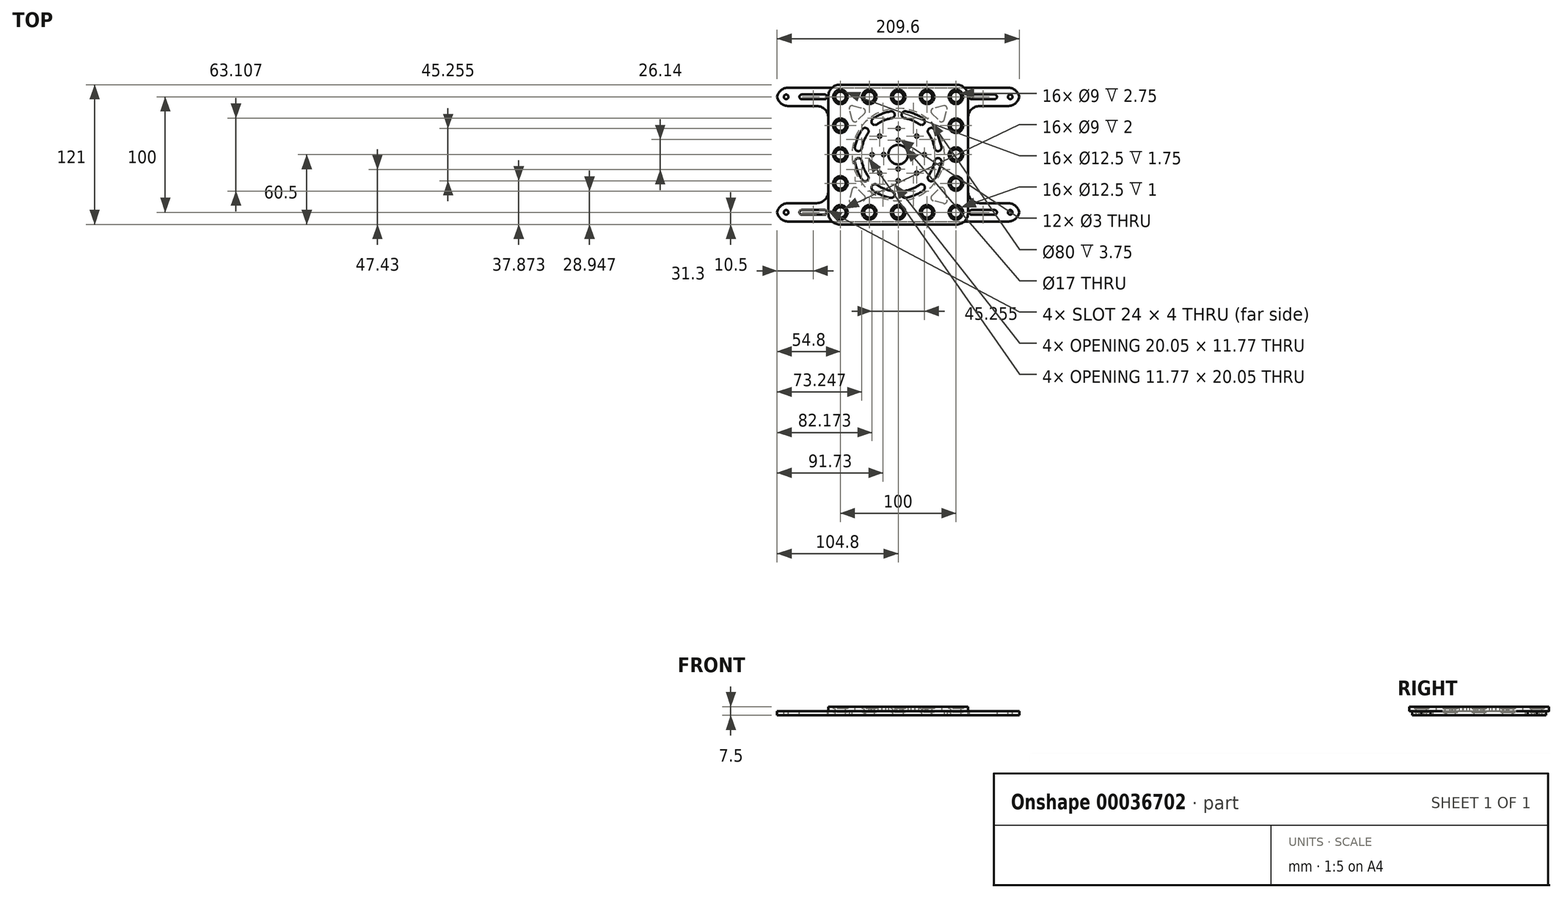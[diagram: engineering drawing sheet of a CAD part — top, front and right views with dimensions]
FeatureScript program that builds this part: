
annotation { "Feature Type Name" : "Feature", "Feature Type Description" : "" }
export const myFeature = defineFeature(function(context is Context, id is Id, definition is map)
    precondition{}
    {
        {
            var Q0;
            Q0=qCreatedBy(makeId("Top.planeOp"),FACE);
            var sketch = newSketch(context, id + "F0", { "sketchPlane" : qUnion([Q0])});
            skPoint(sketch, "E0.rect.middle", {"position": v(0, 0) * mm});
            skCircle(sketch, "E1", {"center": v(0, 0) * mm, "radius": 40 * mm});
            skLineSegment(sketch, "E2.rect.bottom", {"start": v(-50, 50) * mm, "end": v(50, 50) * mm, "construction": true});
            skLineSegment(sketch, "E2.rect.top", {"start": v(-50, -50) * mm, "end": v(50, -50) * mm, "construction": true});
            skLineSegment(sketch, "E2.rect.left", {"start": v(-50, 50) * mm, "end": v(-50, -50) * mm, "construction": true});
            skLineSegment(sketch, "E2.rect.right", {"start": v(50, 50) * mm, "end": v(50, -50) * mm, "construction": true});
            skCircle(sketch, "E3", {"center": v(-50, 50) * mm, "radius": 4.5 * mm});
            skCircle(sketch, "E4", {"center": v(50, 50) * mm, "radius": 4.5 * mm});
            skCircle(sketch, "E5", {"center": v(50, -50) * mm, "radius": 4.5 * mm});
            skCircle(sketch, "E6", {"center": v(-50, -50) * mm, "radius": 4.5 * mm});
            skCircle(sketch, "E7", {"center": v(0, -50) * mm, "radius": 4.5 * mm});
            skCircle(sketch, "E8", {"center": v(0, 50) * mm, "radius": 4.5 * mm});
            skCircle(sketch, "E9", {"center": v(50, 0) * mm, "radius": 4.5 * mm});
            skCircle(sketch, "E10", {"center": v(-50, 0) * mm, "radius": 4.5 * mm});
            skLineSegment(sketch, "E11.rect.bottom", {"start": v(-50, 25) * mm, "end": v(50, 25) * mm, "construction": true});
            skLineSegment(sketch, "E11.rect.top", {"start": v(-50, -25) * mm, "end": v(50, -25) * mm, "construction": true});
            skLineSegment(sketch, "E11.rect.left", {"start": v(-50, 25) * mm, "end": v(-50, -25) * mm, "construction": true});
            skLineSegment(sketch, "E11.rect.right", {"start": v(50, 25) * mm, "end": v(50, -25) * mm, "construction": true});
            skCircle(sketch, "E12", {"center": v(-50, 25) * mm, "radius": 4.5 * mm});
            skCircle(sketch, "E13", {"center": v(50, 25) * mm, "radius": 4.5 * mm});
            skCircle(sketch, "E14", {"center": v(50, -25) * mm, "radius": 4.5 * mm});
            skCircle(sketch, "E15", {"center": v(-50, -25) * mm, "radius": 4.5 * mm});
            skLineSegment(sketch, "E16.rect.bottom", {"start": v(-25, 50) * mm, "end": v(25, 50) * mm, "construction": true});
            skLineSegment(sketch, "E16.rect.top", {"start": v(-25, -50) * mm, "end": v(25, -50) * mm, "construction": true});
            skLineSegment(sketch, "E16.rect.left", {"start": v(-25, 50) * mm, "end": v(-25, -50) * mm, "construction": true});
            skLineSegment(sketch, "E16.rect.right", {"start": v(25, 50) * mm, "end": v(25, -50) * mm, "construction": true});
            skCircle(sketch, "E17", {"center": v(-25, 50) * mm, "radius": 4.5 * mm});
            skCircle(sketch, "E18", {"center": v(25, 50) * mm, "radius": 4.5 * mm});
            skCircle(sketch, "E19", {"center": v(25, -50) * mm, "radius": 4.5 * mm});
            skCircle(sketch, "E20", {"center": v(-25, -50) * mm, "radius": 4.5 * mm});
            skLineSegment(sketch, "E21.rect.bottom", {"start": v(-105, 58) * mm, "end": v(105, 58) * mm});
            skLineSegment(sketch, "E21.rect.top", {"start": v(-105, -58) * mm, "end": v(105, -58) * mm});
            skLineSegment(sketch, "E21.rect.left", {"start": v(-105, 58) * mm, "end": v(-105, 42) * mm});
            skLineSegment(sketch, "E21.rect.right", {"start": v(105, 58) * mm, "end": v(105, 42) * mm});
            skLineSegment(sketch, "E22.rect.bottom", {"start": v(-97, 50) * mm, "end": v(97, 50) * mm, "construction": true});
            skLineSegment(sketch, "E22.rect.top", {"start": v(-97, -50) * mm, "end": v(97, -50) * mm, "construction": true});
            skLineSegment(sketch, "E22.rect.left", {"start": v(-97, 50) * mm, "end": v(-97, -50) * mm, "construction": true});
            skLineSegment(sketch, "E22.rect.right", {"start": v(97, 50) * mm, "end": v(97, -50) * mm, "construction": true});
            skCircle(sketch, "E23", {"center": v(-97, 50) * mm, "radius": 2 * mm});
            skCircle(sketch, "E24", {"center": v(-97, -50) * mm, "radius": 2 * mm});
            skCircle(sketch, "E25", {"center": v(97, -50) * mm, "radius": 2 * mm});
            skCircle(sketch, "E26", {"center": v(97, 50) * mm, "radius": 2 * mm});
            skPoint(sketch, "E27", {"position": v(-105, 0) * mm});
            skLineSegment(sketch, "E28", {"start": v(-97, 48) * mm, "end": v(-97, 42) * mm, "construction": true});
            skLineSegment(sketch, "E29", {"start": v(0, 58) * mm, "end": v(0, -58) * mm});
            skLineSegment(sketch, "E30", {"start": v(-50, 50) * mm, "end": v(50, -50) * mm, "construction": true});
            skLineSegment(sketch, "E31", {"start": v(-50, -50) * mm, "end": v(50, 50) * mm, "construction": true});
            skLineSegment(sketch, "E32", {"start": v(-105, -42) * mm, "end": v(-105, -58) * mm});
            skLineSegment(sketch, "E33", {"start": v(-65, 0) * mm, "end": v(100, 0) * mm, "construction": true});
            skLineSegment(sketch, "E34", {"start": v(105, -42) * mm, "end": v(105, -58) * mm});
            skCircle(sketch, "E35", {"center": v(0, 0) * mm, "radius": 51 * mm, "construction": true});
            skCircle(sketch, "E36.cCircle", {"center": v(-36.06, 36.06) * mm, "radius": 10.4 * mm, "construction": true});
            skLineSegment(sketch, "E36.0", {"start": v(-43.41, 43.41) * mm, "end": v(-26.02, 38.75) * mm});
            skLineSegment(sketch, "E36.1", {"start": v(-26.02, 38.75) * mm, "end": v(-38.75, 26.02) * mm});
            skLineSegment(sketch, "E36.2", {"start": v(-38.75, 26.02) * mm, "end": v(-43.41, 43.41) * mm});
            skLineSegment(sketch, "E37.MirrorCS", {"start": v(26.02, 38.75) * mm, "end": v(38.75, 26.02) * mm});
            skLineSegment(sketch, "E38.MirrorCS", {"start": v(43.41, 43.41) * mm, "end": v(26.02, 38.75) * mm});
            skLineSegment(sketch, "E39.MirrorCS", {"start": v(38.75, 26.02) * mm, "end": v(43.41, 43.41) * mm});
            skLineSegment(sketch, "E40.MirrorCS", {"start": v(-26.02, -38.75) * mm, "end": v(-38.75, -26.02) * mm});
            skLineSegment(sketch, "E41.MirrorCS", {"start": v(-43.41, -43.41) * mm, "end": v(-26.02, -38.75) * mm});
            skLineSegment(sketch, "E42.MirrorCS", {"start": v(-38.75, -26.02) * mm, "end": v(-43.41, -43.41) * mm});
            skLineSegment(sketch, "E43.MirrorCS", {"start": v(26.02, -38.75) * mm, "end": v(38.75, -26.02) * mm});
            skLineSegment(sketch, "E44.MirrorCS", {"start": v(43.41, -43.41) * mm, "end": v(26.02, -38.75) * mm});
            skLineSegment(sketch, "E45.MirrorCS", {"start": v(38.75, -26.02) * mm, "end": v(43.41, -43.41) * mm});
            skLineSegment(sketch, "E46", {"start": v(-97, 50) * mm, "end": v(-50, 50) * mm});
            skPoint(sketch, "E47", {"position": v(-73.5, 50) * mm});
            skLineSegment(sketch, "E48.rect.bottom", {"start": v(-85.5, 48) * mm, "end": v(-61.5, 48) * mm});
            skLineSegment(sketch, "E48.rect.top", {"start": v(-85.5, 52) * mm, "end": v(-61.5, 52) * mm});
            skLineSegment(sketch, "E48.rect.left", {"start": v(-85.5, 48) * mm, "end": v(-85.5, 52) * mm});
            skLineSegment(sketch, "E48.rect.right", {"start": v(-61.5, 48) * mm, "end": v(-61.5, 52) * mm});
            skLineSegment(sketch, "E49.MirrorCS", {"start": v(85.5, 48) * mm, "end": v(61.5, 48) * mm});
            skLineSegment(sketch, "E50.MirrorCS", {"start": v(85.5, 52) * mm, "end": v(61.5, 52) * mm});
            skLineSegment(sketch, "E51.MirrorCS", {"start": v(85.5, 48) * mm, "end": v(85.5, 52) * mm});
            skLineSegment(sketch, "E52.MirrorCS", {"start": v(61.5, 48) * mm, "end": v(61.5, 52) * mm});
            skLineSegment(sketch, "E53.MirrorCS", {"start": v(-85.5, -48) * mm, "end": v(-61.5, -48) * mm});
            skLineSegment(sketch, "E54.MirrorCS", {"start": v(-85.5, -52) * mm, "end": v(-61.5, -52) * mm});
            skLineSegment(sketch, "E55.MirrorCS", {"start": v(-85.5, -48) * mm, "end": v(-85.5, -52) * mm});
            skLineSegment(sketch, "E56.MirrorCS", {"start": v(-61.5, -48) * mm, "end": v(-61.5, -52) * mm});
            skLineSegment(sketch, "E57.MirrorCS", {"start": v(85.5, -48) * mm, "end": v(61.5, -48) * mm});
            skLineSegment(sketch, "E58.MirrorCS", {"start": v(85.5, -52) * mm, "end": v(61.5, -52) * mm});
            skLineSegment(sketch, "E59.MirrorCS", {"start": v(61.5, -48) * mm, "end": v(61.5, -52) * mm});
            skLineSegment(sketch, "E60.MirrorCS", {"start": v(85.5, -48) * mm, "end": v(85.5, -52) * mm});
            skLineSegment(sketch, "E61.right", {"start": v(-60.5, 42) * mm, "end": v(-60.5, -42) * mm});
            skLineSegment(sketch, "E62.MirrorCS", {"start": v(60.5, 42) * mm, "end": v(60.5, -42) * mm});
            skLineSegment(sketch, "E63", {"start": v(-105, -42) * mm, "end": v(-60.5, -42) * mm});
            skLineSegment(sketch, "E64", {"start": v(-105, 42) * mm, "end": v(-60.5, 42) * mm});
            skLineSegment(sketch, "E65", {"start": v(60.5, 42) * mm, "end": v(105, 42) * mm});
            skLineSegment(sketch, "E66", {"start": v(60.5, -42) * mm, "end": v(105, -42) * mm});
            skLineSegment(sketch, "E67", {"start": v(36.06, 36.06) * mm, "end": v(0, 0) * mm});
            skLineSegment(sketch, "E68", {"start": v(-73.5, 50) * mm, "end": v(0, 50) * mm, "construction": true});
            skSolve(sketch);
        }
        {
            var Q0;
            Q0=qSketchRegion(id+"F0",true);
            extrude(context, id + "F1", {"entities" : qUnion([Q0]), "oppositeDirection" : true, "depth" : 3.75 * mm});
        }
        {
            var Q0;
            Q0=makeQuery(id+"F1.opExtrude","SWEPT_EDGE",EDGE,{"disambiguationData":[OSD([sQuery(id+"F0.wireOp",EDGE,"E21.rect.bottom"),sQuery(id+"F0.wireOp",EDGE,"E21.rect.left")])]});
            var Q1;
            Q1=makeQuery(id+"F1.opExtrude","SWEPT_EDGE",EDGE,{"disambiguationData":[OSD([sQuery(id+"F0.wireOp",EDGE,"E21.rect.left"),sQuery(id+"F0.wireOp",EDGE,"4bd72445-ccac-4010-9492-ce205e554f92.top")])]});
            var Q2;
            Q2=makeQuery(id+"F1.opExtrude","SWEPT_EDGE",EDGE,{"disambiguationData":[OSD([sQuery(id+"F0.wireOp",EDGE,"1782753d-d1cd-43f3-90b6-b2e425ba2ceb.top"),sQuery(id+"F0.wireOp",EDGE,"E32")])]});
            var Q3;
            Q3=makeQuery(id+"F1.opExtrude","SWEPT_EDGE",EDGE,{"disambiguationData":[OSD([sQuery(id+"F0.wireOp",EDGE,"E21.rect.top"),sQuery(id+"F0.wireOp",EDGE,"E32")])]});
            var Q4;
            Q4=makeQuery(id+"F1.opExtrude","SWEPT_EDGE",EDGE,{"disambiguationData":[OSD([sQuery(id+"F0.wireOp",EDGE,"7d6b432d-c6f7-4929-92ba-03f9c5655b390.MirrorCS"),sQuery(id+"F0.wireOp",EDGE,"E34")])]});
            var Q5;
            Q5=makeQuery(id+"F1.opExtrude","SWEPT_EDGE",EDGE,{"disambiguationData":[OSD([sQuery(id+"F0.wireOp",EDGE,"E21.rect.bottom"),sQuery(id+"F0.wireOp",EDGE,"E21.rect.right")])]});
            var Q6;
            Q6=makeQuery(id+"F1.opExtrude","SWEPT_EDGE",EDGE,{"disambiguationData":[OSD([sQuery(id+"F0.wireOp",EDGE,"E21.rect.top"),sQuery(id+"F0.wireOp",EDGE,"E34")])]});
            var Q7;
            Q7=makeQuery(id+"F1.opExtrude","SWEPT_EDGE",EDGE,{"disambiguationData":[OSD([sQuery(id+"F0.wireOp",EDGE,"E21.rect.right"),sQuery(id+"F0.wireOp",EDGE,"df5098c2-97dc-40db-a8c1-e7d122068beb0.MirrorCS")])]});
            fillet(context, id + "F2", {"entities" : qUnion([Q0, Q1, Q2, Q3, Q4, Q5, Q6, Q7]), "radius" : 10 * mm, "tangentPropagation" : true, "allowEdgeOverflow" : false});
        }
        {
            var Q0;
            Q0=makeQuery(id+"F1.opExtrude","SWEPT_EDGE",EDGE,{"disambiguationData":[OSD([sQuery(id+"F0.wireOp",EDGE,"E36.1"),sQuery(id+"F0.wireOp",EDGE,"E36.2")])]});
            var Q1;
            Q1=makeQuery(id+"F1.opExtrude","SWEPT_EDGE",EDGE,{"disambiguationData":[OSD([sQuery(id+"F0.wireOp",EDGE,"E36.0"),sQuery(id+"F0.wireOp",EDGE,"E36.2")])]});
            var Q2;
            Q2=makeQuery(id+"F1.opExtrude","SWEPT_EDGE",EDGE,{"disambiguationData":[OSD([sQuery(id+"F0.wireOp",EDGE,"E36.0"),sQuery(id+"F0.wireOp",EDGE,"E36.1")])]});
            var Q3;
            Q3=makeQuery(id+"F1.opExtrude","SWEPT_EDGE",EDGE,{"disambiguationData":[OSD([sQuery(id+"F0.wireOp",EDGE,"E40.MirrorCS"),sQuery(id+"F0.wireOp",EDGE,"E42.MirrorCS")])]});
            var Q4;
            Q4=makeQuery(id+"F1.opExtrude","SWEPT_EDGE",EDGE,{"disambiguationData":[OSD([sQuery(id+"F0.wireOp",EDGE,"E43.MirrorCS"),sQuery(id+"F0.wireOp",EDGE,"E45.MirrorCS")])]});
            var Q5;
            Q5=makeQuery(id+"F1.opExtrude","SWEPT_EDGE",EDGE,{"disambiguationData":[OSD([sQuery(id+"F0.wireOp",EDGE,"E38.MirrorCS"),sQuery(id+"F0.wireOp",EDGE,"E39.MirrorCS")])]});
            var Q6;
            Q6=makeQuery(id+"F1.opExtrude","SWEPT_EDGE",EDGE,{"disambiguationData":[OSD([sQuery(id+"F0.wireOp",EDGE,"E37.MirrorCS"),sQuery(id+"F0.wireOp",EDGE,"E39.MirrorCS")])]});
            var Q7;
            Q7=makeQuery(id+"F1.opExtrude","SWEPT_EDGE",EDGE,{"disambiguationData":[OSD([sQuery(id+"F0.wireOp",EDGE,"E44.MirrorCS"),sQuery(id+"F0.wireOp",EDGE,"E45.MirrorCS")])]});
            var Q8;
            Q8=makeQuery(id+"F1.opExtrude","SWEPT_EDGE",EDGE,{"disambiguationData":[OSD([sQuery(id+"F0.wireOp",EDGE,"E41.MirrorCS"),sQuery(id+"F0.wireOp",EDGE,"E42.MirrorCS")])]});
            var Q9;
            Q9=makeQuery(id+"F1.opExtrude","SWEPT_EDGE",EDGE,{"disambiguationData":[OSD([sQuery(id+"F0.wireOp",EDGE,"E37.MirrorCS"),sQuery(id+"F0.wireOp",EDGE,"E38.MirrorCS")])]});
            var Q10;
            Q10=makeQuery(id+"F1.opExtrude","SWEPT_EDGE",EDGE,{"disambiguationData":[OSD([sQuery(id+"F0.wireOp",EDGE,"E43.MirrorCS"),sQuery(id+"F0.wireOp",EDGE,"E44.MirrorCS")])]});
            var Q11;
            Q11=makeQuery(id+"F1.opExtrude","SWEPT_EDGE",EDGE,{"disambiguationData":[OSD([sQuery(id+"F0.wireOp",EDGE,"E40.MirrorCS"),sQuery(id+"F0.wireOp",EDGE,"E41.MirrorCS")])]});
            fillet(context, id + "F3", {"entities" : qUnion([Q0, Q1, Q2, Q3, Q4, Q5, Q6, Q7, Q8, Q9, Q10, Q11]), "radius" : 2.5 * mm, "tangentPropagation" : true, "allowEdgeOverflow" : false});
        }
        {
            var Q0;
            Q0=makeQuery(id+"F1.opExtrude","SWEPT_EDGE",EDGE,{"disambiguationData":[OSD([sQuery(id+"F0.wireOp",EDGE,"E48.rect.top"),sQuery(id+"F0.wireOp",EDGE,"E48.rect.left")])]});
            var Q1;
            Q1=makeQuery(id+"F1.opExtrude","SWEPT_EDGE",EDGE,{"disambiguationData":[OSD([sQuery(id+"F0.wireOp",EDGE,"E48.rect.top"),sQuery(id+"F0.wireOp",EDGE,"E48.rect.right")])]});
            var Q2;
            Q2=makeQuery(id+"F1.opExtrude","SWEPT_EDGE",EDGE,{"disambiguationData":[OSD([sQuery(id+"F0.wireOp",EDGE,"E48.rect.bottom"),sQuery(id+"F0.wireOp",EDGE,"E48.rect.right")])]});
            var Q3;
            Q3=makeQuery(id+"F1.opExtrude","SWEPT_EDGE",EDGE,{"disambiguationData":[OSD([sQuery(id+"F0.wireOp",EDGE,"E48.rect.bottom"),sQuery(id+"F0.wireOp",EDGE,"E48.rect.left")])]});
            var Q4;
            Q4=makeQuery(id+"F1.opExtrude","SWEPT_EDGE",EDGE,{"disambiguationData":[OSD([sQuery(id+"F0.wireOp",EDGE,"E53.MirrorCS"),sQuery(id+"F0.wireOp",EDGE,"E55.MirrorCS")])]});
            var Q5;
            Q5=makeQuery(id+"F1.opExtrude","SWEPT_EDGE",EDGE,{"disambiguationData":[OSD([sQuery(id+"F0.wireOp",EDGE,"E50.MirrorCS"),sQuery(id+"F0.wireOp",EDGE,"E52.MirrorCS")])]});
            var Q6;
            Q6=makeQuery(id+"F1.opExtrude","SWEPT_EDGE",EDGE,{"disambiguationData":[OSD([sQuery(id+"F0.wireOp",EDGE,"E57.MirrorCS"),sQuery(id+"F0.wireOp",EDGE,"E59.MirrorCS")])]});
            var Q7;
            Q7=makeQuery(id+"F1.opExtrude","SWEPT_EDGE",EDGE,{"disambiguationData":[OSD([sQuery(id+"F0.wireOp",EDGE,"E57.MirrorCS"),sQuery(id+"F0.wireOp",EDGE,"E60.MirrorCS")])]});
            var Q8;
            Q8=makeQuery(id+"F1.opExtrude","SWEPT_EDGE",EDGE,{"disambiguationData":[OSD([sQuery(id+"F0.wireOp",EDGE,"E53.MirrorCS"),sQuery(id+"F0.wireOp",EDGE,"E56.MirrorCS")])]});
            var Q9;
            Q9=makeQuery(id+"F1.opExtrude","SWEPT_EDGE",EDGE,{"disambiguationData":[OSD([sQuery(id+"F0.wireOp",EDGE,"E50.MirrorCS"),sQuery(id+"F0.wireOp",EDGE,"E51.MirrorCS")])]});
            var Q10;
            Q10=makeQuery(id+"F1.opExtrude","SWEPT_EDGE",EDGE,{"disambiguationData":[OSD([sQuery(id+"F0.wireOp",EDGE,"E54.MirrorCS"),sQuery(id+"F0.wireOp",EDGE,"E55.MirrorCS")])]});
            var Q11;
            Q11=makeQuery(id+"F1.opExtrude","SWEPT_EDGE",EDGE,{"disambiguationData":[OSD([sQuery(id+"F0.wireOp",EDGE,"E49.MirrorCS"),sQuery(id+"F0.wireOp",EDGE,"E52.MirrorCS")])]});
            var Q12;
            Q12=makeQuery(id+"F1.opExtrude","SWEPT_EDGE",EDGE,{"disambiguationData":[OSD([sQuery(id+"F0.wireOp",EDGE,"E58.MirrorCS"),sQuery(id+"F0.wireOp",EDGE,"E59.MirrorCS")])]});
            var Q13;
            Q13=makeQuery(id+"F1.opExtrude","SWEPT_EDGE",EDGE,{"disambiguationData":[OSD([sQuery(id+"F0.wireOp",EDGE,"E54.MirrorCS"),sQuery(id+"F0.wireOp",EDGE,"E56.MirrorCS")])]});
            var Q14;
            Q14=makeQuery(id+"F1.opExtrude","SWEPT_EDGE",EDGE,{"disambiguationData":[OSD([sQuery(id+"F0.wireOp",EDGE,"E58.MirrorCS"),sQuery(id+"F0.wireOp",EDGE,"E60.MirrorCS")])]});
            var Q15;
            Q15=makeQuery(id+"F1.opExtrude","SWEPT_EDGE",EDGE,{"disambiguationData":[OSD([sQuery(id+"F0.wireOp",EDGE,"E49.MirrorCS"),sQuery(id+"F0.wireOp",EDGE,"E51.MirrorCS")])]});
            fillet(context, id + "F4", {"entities" : qUnion([Q0, Q1, Q2, Q3, Q4, Q5, Q6, Q7, Q8, Q9, Q10, Q11, Q12, Q13, Q14, Q15]), "radius" : 2 * mm, "tangentPropagation" : true, "allowEdgeOverflow" : false});
        }
        {
            var Q0;
            Q0=qCreatedBy(makeId("Top.planeOp"),FACE);
            var sketch = newSketch(context, id + "F5", { "sketchPlane" : qUnion([Q0])});
            skLineSegment(sketch, "E69.rect.bottom", {"start": v(-60.5, 60.5) * mm, "end": v(60.5, 60.5) * mm});
            skLineSegment(sketch, "E69.rect.top", {"start": v(-60.5, -60.5) * mm, "end": v(60.5, -60.5) * mm});
            skLineSegment(sketch, "E69.rect.left", {"start": v(-60.5, 60.5) * mm, "end": v(-60.5, -60.5) * mm});
            skLineSegment(sketch, "E69.rect.right", {"start": v(60.5, 60.5) * mm, "end": v(60.5, -60.5) * mm});
            skPoint(sketch, "E69.rect.middle", {"position": v(0, 0) * mm});
            skSolve(sketch);
        }
        {
            var Q0;
            Q0=qCreatedBy(makeId("Top.planeOp"),FACE);
            var sketch = newSketch(context, id + "F6", { "sketchPlane" : qUnion([Q0])});
            skPoint(sketch, "E70.0", {"position": v(-50, 50) * mm});
            skCircle(sketch, "E70.1", {"center": v(-50, 50) * mm, "radius": 4.5 * mm});
            skCircle(sketch, "E71", {"center": v(-50, 50) * mm, "radius": 6.25 * mm});
            skCircle(sketch, "E72.0", {"center": v(-25, 50) * mm, "radius": 4.5 * mm});
            skCircle(sketch, "E72.1", {"center": v(0, 50) * mm, "radius": 4.5 * mm});
            skCircle(sketch, "E72.2", {"center": v(25, 50) * mm, "radius": 4.5 * mm});
            skCircle(sketch, "E72.3", {"center": v(50, 50) * mm, "radius": 4.5 * mm});
            skCircle(sketch, "E72.4", {"center": v(50, 25) * mm, "radius": 4.5 * mm});
            skCircle(sketch, "E72.5", {"center": v(50, 0) * mm, "radius": 4.5 * mm});
            skCircle(sketch, "E72.6", {"center": v(50, -25) * mm, "radius": 4.5 * mm});
            skCircle(sketch, "E72.7", {"center": v(50, -50) * mm, "radius": 4.5 * mm});
            skCircle(sketch, "E72.8", {"center": v(25, -50) * mm, "radius": 4.5 * mm});
            skCircle(sketch, "E72.9", {"center": v(0, -50) * mm, "radius": 4.5 * mm});
            skCircle(sketch, "E72.10", {"center": v(-25, -50) * mm, "radius": 4.5 * mm});
            skCircle(sketch, "E72.11", {"center": v(-50, -50) * mm, "radius": 4.5 * mm});
            skCircle(sketch, "E72.12", {"center": v(-50, -25) * mm, "radius": 4.5 * mm});
            skCircle(sketch, "E72.13", {"center": v(-50, 0) * mm, "radius": 4.5 * mm});
            skCircle(sketch, "E72.14", {"center": v(-50, 25) * mm, "radius": 4.5 * mm});
            skCircle(sketch, "E73.0.1.0", {"center": v(-50, 25) * mm, "radius": 6.25 * mm});
            skCircle(sketch, "E73.0.2.0", {"center": v(-50, 0) * mm, "radius": 6.25 * mm});
            skCircle(sketch, "E73.0.3.0", {"center": v(-50, -25) * mm, "radius": 6.25 * mm});
            skCircle(sketch, "E73.0.4.0", {"center": v(-50, -50) * mm, "radius": 6.25 * mm});
            skCircle(sketch, "E73.1.0.0", {"center": v(-25, 50) * mm, "radius": 6.25 * mm});
            skCircle(sketch, "E73.1.4.0", {"center": v(-25, -50) * mm, "radius": 6.25 * mm});
            skCircle(sketch, "E73.2.0.0", {"center": v(0, 50) * mm, "radius": 6.25 * mm});
            skCircle(sketch, "E73.2.4.0", {"center": v(0, -50) * mm, "radius": 6.25 * mm});
            skCircle(sketch, "E73.3.0.0", {"center": v(25, 50) * mm, "radius": 6.25 * mm});
            skCircle(sketch, "E73.3.4.0", {"center": v(25, -50) * mm, "radius": 6.25 * mm});
            skCircle(sketch, "E73.4.0.0", {"center": v(50, 50) * mm, "radius": 6.25 * mm});
            skCircle(sketch, "E73.4.1.0", {"center": v(50, 25) * mm, "radius": 6.25 * mm});
            skCircle(sketch, "E73.4.2.0", {"center": v(50, 0) * mm, "radius": 6.25 * mm});
            skCircle(sketch, "E73.4.3.0", {"center": v(50, -25) * mm, "radius": 6.25 * mm});
            skCircle(sketch, "E73.4.4.0", {"center": v(50, -50) * mm, "radius": 6.25 * mm});
            skLineSegment(sketch, "E73.direction1", {"start": v(-50, 50) * mm, "end": v(-25, 50) * mm, "construction": true});
            skLineSegment(sketch, "E73.direction2", {"start": v(-50, 50) * mm, "end": v(-50, 25) * mm, "construction": true});
            skSolve(sketch);
        }
        {
            var Q0;
            Q0=qCreatedBy(makeId("Top.planeOp"),FACE);
            var sketch = newSketch(context, id + "F7", { "sketchPlane" : qUnion([Q0])});
            skPoint(sketch, "E74.0", {"position": v(-0.06, -0.04) * mm});
            skCircle(sketch, "E75", {"center": v(0, 0) * mm, "radius": 38 * mm, "construction": true});
            skLineSegment(sketch, "E76.0", {"start": v(0, 6) * mm, "end": v(-38, 6) * mm, "construction": true});
            skLineSegment(sketch, "E77.0", {"start": v(0, -6) * mm, "end": v(-38, -6) * mm, "construction": true});
            skArc(sketch, "E78", {"start": v(-34.48, 6) * mm, "mid": v(-35, 0) * mm, "end": v(-34.48, -6) * mm, "construction": true});
            skArc(sketch, "E79", {"start": v(-34.48, -6) * mm, "mid": v(32.34, -13.4) * mm, "end": v(-20.14, 28.63) * mm, "construction": true});
            skLineSegment(sketch, "E80.1.0", {"start": v(-4.24, 4.24) * mm, "end": v(-31.11, -22.63) * mm, "construction": true});
            skLineSegment(sketch, "E80.2.0", {"start": v(-6, 0) * mm, "end": v(-6, -38) * mm, "construction": true});
            skLineSegment(sketch, "E80.3.0", {"start": v(-4.24, -4.24) * mm, "end": v(22.63, -31.11) * mm, "construction": true});
            skLineSegment(sketch, "E80.4.0", {"start": v(0, -6) * mm, "end": v(38, -6) * mm, "construction": true});
            skLineSegment(sketch, "E80.5.0", {"start": v(4.24, -4.24) * mm, "end": v(31.11, 22.63) * mm, "construction": true});
            skLineSegment(sketch, "E80.6.0", {"start": v(6, 0) * mm, "end": v(6, 38) * mm, "construction": true});
            skLineSegment(sketch, "E80.7.0", {"start": v(4.24, 4.24) * mm, "end": v(-22.63, 31.11) * mm, "construction": true});
            skArc(sketch, "E81", {"start": v(-20.14, 28.63) * mm, "mid": v(-24.75, 24.75) * mm, "end": v(-28.63, 20.14) * mm, "construction": true});
            skLineSegment(sketch, "E82.1.0", {"start": v(4.24, -4.24) * mm, "end": v(-22.63, -31.11) * mm, "construction": true});
            skLineSegment(sketch, "E82.2.0", {"start": v(6, 0) * mm, "end": v(6, -38) * mm, "construction": true});
            skLineSegment(sketch, "E82.3.0", {"start": v(4.24, 4.24) * mm, "end": v(31.11, -22.63) * mm, "construction": true});
            skLineSegment(sketch, "E82.4.0", {"start": v(0, 6) * mm, "end": v(38, 6) * mm, "construction": true});
            skLineSegment(sketch, "E82.5.0", {"start": v(-4.24, 4.24) * mm, "end": v(22.63, 31.11) * mm, "construction": true});
            skLineSegment(sketch, "E82.6.0", {"start": v(-6, 0) * mm, "end": v(-6, 38) * mm, "construction": true});
            skLineSegment(sketch, "E82.7.0", {"start": v(-4.24, -4.24) * mm, "end": v(-31.11, 22.63) * mm, "construction": true});
            skArc(sketch, "E83", {"start": v(-28.63, 20.14) * mm, "mid": v(-32.34, 13.4) * mm, "end": v(-34.48, 6) * mm, "construction": true});
            skArc(sketch, "E84.0.startCap", {"start": v(-31.08, 21.87) * mm, "mid": v(-26.9, 22.6) * mm, "end": v(-26.17, 18.41) * mm});
            skArc(sketch, "E84.0.endCap", {"start": v(-31.53, 5.49) * mm, "mid": v(-35, 3.04) * mm, "end": v(-37.44, 6.51) * mm});
            skArc(sketch, "E84.0.left", {"start": v(-26.17, 18.41) * mm, "mid": v(-29.56, 12.25) * mm, "end": v(-31.53, 5.49) * mm});
            skArc(sketch, "E84.0.right", {"start": v(-31.08, 21.87) * mm, "mid": v(-35.1, 14.54) * mm, "end": v(-37.44, 6.51) * mm});
            skArc(sketch, "E85.1.0", {"start": v(-26.17, -18.41) * mm, "mid": v(-26.9, -22.6) * mm, "end": v(-31.08, -21.87) * mm});
            skArc(sketch, "E85.1.1", {"start": v(-37.44, -6.51) * mm, "mid": v(-35.1, -14.54) * mm, "end": v(-31.08, -21.87) * mm});
            skArc(sketch, "E85.1.2", {"start": v(-37.44, -6.51) * mm, "mid": v(-35, -3.04) * mm, "end": v(-31.53, -5.49) * mm});
            skArc(sketch, "E85.1.3", {"start": v(-31.53, -5.49) * mm, "mid": v(-29.56, -12.25) * mm, "end": v(-26.17, -18.41) * mm});
            skArc(sketch, "E85.2.0", {"start": v(-5.49, -31.53) * mm, "mid": v(-3.04, -35) * mm, "end": v(-6.51, -37.44) * mm});
            skArc(sketch, "E85.2.1", {"start": v(-21.87, -31.08) * mm, "mid": v(-14.54, -35.1) * mm, "end": v(-6.51, -37.44) * mm});
            skArc(sketch, "E85.2.2", {"start": v(-21.87, -31.08) * mm, "mid": v(-22.6, -26.9) * mm, "end": v(-18.41, -26.17) * mm});
            skArc(sketch, "E85.2.3", {"start": v(-18.41, -26.17) * mm, "mid": v(-12.25, -29.56) * mm, "end": v(-5.49, -31.53) * mm});
            skArc(sketch, "E85.3.0", {"start": v(18.41, -26.17) * mm, "mid": v(22.6, -26.9) * mm, "end": v(21.87, -31.08) * mm});
            skArc(sketch, "E85.3.1", {"start": v(6.51, -37.44) * mm, "mid": v(14.54, -35.1) * mm, "end": v(21.87, -31.08) * mm});
            skArc(sketch, "E85.3.2", {"start": v(6.51, -37.44) * mm, "mid": v(3.04, -35) * mm, "end": v(5.49, -31.53) * mm});
            skArc(sketch, "E85.3.3", {"start": v(5.49, -31.53) * mm, "mid": v(12.25, -29.56) * mm, "end": v(18.41, -26.17) * mm});
            skArc(sketch, "E85.4.0", {"start": v(31.53, -5.49) * mm, "mid": v(35, -3.04) * mm, "end": v(37.44, -6.51) * mm});
            skArc(sketch, "E85.4.1", {"start": v(31.08, -21.87) * mm, "mid": v(35.1, -14.54) * mm, "end": v(37.44, -6.51) * mm});
            skArc(sketch, "E85.4.2", {"start": v(31.08, -21.87) * mm, "mid": v(26.9, -22.6) * mm, "end": v(26.17, -18.41) * mm});
            skArc(sketch, "E85.4.3", {"start": v(26.17, -18.41) * mm, "mid": v(29.56, -12.25) * mm, "end": v(31.53, -5.49) * mm});
            skArc(sketch, "E85.5.0", {"start": v(26.17, 18.41) * mm, "mid": v(26.9, 22.6) * mm, "end": v(31.08, 21.87) * mm});
            skArc(sketch, "E85.5.1", {"start": v(37.44, 6.51) * mm, "mid": v(35.1, 14.54) * mm, "end": v(31.08, 21.87) * mm});
            skArc(sketch, "E85.5.2", {"start": v(37.44, 6.51) * mm, "mid": v(35, 3.04) * mm, "end": v(31.53, 5.49) * mm});
            skArc(sketch, "E85.5.3", {"start": v(31.53, 5.49) * mm, "mid": v(29.56, 12.25) * mm, "end": v(26.17, 18.41) * mm});
            skArc(sketch, "E85.6.0", {"start": v(5.49, 31.53) * mm, "mid": v(3.04, 35) * mm, "end": v(6.51, 37.44) * mm});
            skArc(sketch, "E85.6.1", {"start": v(21.87, 31.08) * mm, "mid": v(14.54, 35.1) * mm, "end": v(6.51, 37.44) * mm});
            skArc(sketch, "E85.6.2", {"start": v(21.87, 31.08) * mm, "mid": v(22.6, 26.9) * mm, "end": v(18.41, 26.17) * mm});
            skArc(sketch, "E85.6.3", {"start": v(18.41, 26.17) * mm, "mid": v(12.25, 29.56) * mm, "end": v(5.49, 31.53) * mm});
            skArc(sketch, "E85.7.0", {"start": v(-18.41, 26.17) * mm, "mid": v(-22.6, 26.9) * mm, "end": v(-21.87, 31.08) * mm});
            skArc(sketch, "E85.7.1", {"start": v(-6.51, 37.44) * mm, "mid": v(-14.54, 35.1) * mm, "end": v(-21.87, 31.08) * mm});
            skArc(sketch, "E85.7.2", {"start": v(-6.51, 37.44) * mm, "mid": v(-3.04, 35) * mm, "end": v(-5.49, 31.53) * mm});
            skArc(sketch, "E85.7.3", {"start": v(-5.49, 31.53) * mm, "mid": v(-12.25, 29.56) * mm, "end": v(-18.41, 26.17) * mm});
            skPoint(sketch, "E86", {"position": v(22.52, 26.8) * mm});
            skPoint(sketch, "E87", {"position": v(26.8, 22.52) * mm});
            skLineSegment(sketch, "E88", {"start": v(22.52, 26.8) * mm, "end": v(26.8, 22.52) * mm});
            skSolve(sketch);
        }
        {
            var Q0;
            Q0=qCreatedBy(makeId("Top.planeOp"),FACE);
            var sketch = newSketch(context, id + "F8", { "sketchPlane" : qUnion([Q0])});
            skPoint(sketch, "E89.rect.middle", {"position": v(0, 0) * mm});
            skCircle(sketch, "E90", {"center": v(0, 0) * mm, "radius": 8.5 * mm});
            skLineSegment(sketch, "E91.rect.bottom", {"start": v(-16, 16) * mm, "end": v(16, 16) * mm, "construction": true});
            skLineSegment(sketch, "E91.rect.top", {"start": v(-16, -16) * mm, "end": v(16, -16) * mm, "construction": true});
            skLineSegment(sketch, "E91.rect.left", {"start": v(-16, 16) * mm, "end": v(-16, -16) * mm, "construction": true});
            skLineSegment(sketch, "E91.rect.right", {"start": v(16, 16) * mm, "end": v(16, -16) * mm, "construction": true});
            skCircle(sketch, "E92", {"center": v(-16, -16) * mm, "radius": 1.5 * mm});
            skCircle(sketch, "E93.1.0", {"center": v(0, -22.63) * mm, "radius": 1.5 * mm});
            skCircle(sketch, "E93.2.0", {"center": v(16, -16) * mm, "radius": 1.5 * mm});
            skCircle(sketch, "E93.3.0", {"center": v(22.63, 0) * mm, "radius": 1.5 * mm});
            skCircle(sketch, "E93.4.0", {"center": v(16, 16) * mm, "radius": 1.5 * mm});
            skCircle(sketch, "E93.5.0", {"center": v(0, 22.63) * mm, "radius": 1.5 * mm});
            skCircle(sketch, "E93.6.0", {"center": v(-16, 16) * mm, "radius": 1.5 * mm});
            skCircle(sketch, "E93.7.0", {"center": v(-22.63, 0) * mm, "radius": 1.5 * mm});
            skCircle(sketch, "E94", {"center": v(0, 0) * mm, "radius": 22.63 * mm, "construction": true});
            skLineSegment(sketch, "E95.rect.bottom", {"start": v(12.5, 12.5) * mm, "end": v(-12.5, 12.5) * mm, "construction": true});
            skLineSegment(sketch, "E95.rect.top", {"start": v(12.5, -12.5) * mm, "end": v(-12.5, -12.5) * mm, "construction": true});
            skLineSegment(sketch, "E95.rect.left", {"start": v(12.5, 12.5) * mm, "end": v(12.5, -12.5) * mm, "construction": true});
            skLineSegment(sketch, "E95.rect.right", {"start": v(-12.5, 12.5) * mm, "end": v(-12.5, -12.5) * mm, "construction": true});
            skCircle(sketch, "E96", {"center": v(-12.5, 0) * mm, "radius": 1.5 * mm});
            skCircle(sketch, "E97", {"center": v(12.5, 0) * mm, "radius": 1.5 * mm});
            skCircle(sketch, "E98", {"center": v(0, 12.5) * mm, "radius": 1.5 * mm});
            skCircle(sketch, "E99", {"center": v(0, -12.5) * mm, "radius": 1.5 * mm});
            skPoint(sketch, "E100.center", {"position": v(-0.06, -0.04) * mm});
            skLineSegment(sketch, "E101.0", {"start": v(2.9, -31.85) * mm, "end": v(2.9, -31.87) * mm});
            skSolve(sketch);
        }
        {
            var Q0;
            Q0=qCreatedBy(makeId("Top.planeOp"),FACE);
            var sketch = newSketch(context, id + "F9", { "sketchPlane" : qUnion([Q0])});
            skArc(sketch, "E102.10", {"start": v(-31.08, 21.87) * mm, "mid": v(-35.1, 14.54) * mm, "end": v(-37.44, 6.51) * mm});
            skArc(sketch, "E102.11", {"start": v(-26.17, 18.41) * mm, "mid": v(-29.56, 12.25) * mm, "end": v(-31.53, 5.49) * mm});
            skArc(sketch, "E102.12", {"start": v(-31.08, 21.87) * mm, "mid": v(-26.9, 22.6) * mm, "end": v(-26.17, 18.41) * mm});
            skArc(sketch, "E102.13", {"start": v(-31.53, 5.49) * mm, "mid": v(-35, 3.04) * mm, "end": v(-37.44, 6.51) * mm});
            skArc(sketch, "E102.14", {"start": v(-5.49, 31.53) * mm, "mid": v(-12.25, 29.56) * mm, "end": v(-18.41, 26.17) * mm});
            skArc(sketch, "E102.15", {"start": v(-6.51, 37.44) * mm, "mid": v(-14.54, 35.1) * mm, "end": v(-21.87, 31.08) * mm});
            skArc(sketch, "E102.16", {"start": v(-18.41, 26.17) * mm, "mid": v(-22.6, 26.9) * mm, "end": v(-21.87, 31.08) * mm});
            skArc(sketch, "E102.17", {"start": v(-6.51, 37.44) * mm, "mid": v(-3.04, 35) * mm, "end": v(-5.49, 31.53) * mm});
            skPoint(sketch, "E102.18", {"position": v(5.49, 31.53) * mm});
            skArc(sketch, "E102.19", {"start": v(5.49, 31.53) * mm, "mid": v(3.04, 35) * mm, "end": v(6.51, 37.44) * mm});
            skArc(sketch, "E102.20", {"start": v(21.87, 31.08) * mm, "mid": v(14.54, 35.1) * mm, "end": v(6.51, 37.44) * mm});
            skArc(sketch, "E102.21", {"start": v(18.41, 26.17) * mm, "mid": v(12.25, 29.56) * mm, "end": v(5.49, 31.53) * mm});
            skArc(sketch, "E102.22", {"start": v(21.87, 31.08) * mm, "mid": v(22.6, 26.9) * mm, "end": v(18.41, 26.17) * mm});
            skArc(sketch, "E102.23", {"start": v(26.17, 18.41) * mm, "mid": v(26.9, 22.6) * mm, "end": v(31.08, 21.87) * mm});
            skArc(sketch, "E102.24", {"start": v(31.53, 5.49) * mm, "mid": v(29.56, 12.25) * mm, "end": v(26.17, 18.41) * mm});
            skArc(sketch, "E102.25", {"start": v(37.44, 6.51) * mm, "mid": v(35.1, 14.54) * mm, "end": v(31.08, 21.87) * mm});
            skArc(sketch, "E102.26", {"start": v(37.44, 6.51) * mm, "mid": v(35, 3.04) * mm, "end": v(31.53, 5.49) * mm});
            skArc(sketch, "E103.0", {"start": v(-37.44, -6.51) * mm, "mid": v(-35.1, -14.54) * mm, "end": v(-31.08, -21.87) * mm});
            skArc(sketch, "E103.1", {"start": v(-31.53, -5.49) * mm, "mid": v(-29.56, -12.25) * mm, "end": v(-26.17, -18.41) * mm});
            skArc(sketch, "E103.2", {"start": v(-37.44, -6.51) * mm, "mid": v(-35, -3.04) * mm, "end": v(-31.53, -5.49) * mm});
            skArc(sketch, "E103.3", {"start": v(-26.17, -18.41) * mm, "mid": v(-26.9, -22.6) * mm, "end": v(-31.08, -21.87) * mm});
            skCircle(sketch, "E104.0", {"center": v(50, 50) * mm, "radius": 6.25 * mm});
            skCircle(sketch, "E104.1", {"center": v(50, 50) * mm, "radius": 4.5 * mm});
            skCircle(sketch, "E104.2", {"center": v(25, 50) * mm, "radius": 6.25 * mm});
            skCircle(sketch, "E104.3", {"center": v(25, 50) * mm, "radius": 4.5 * mm});
            skCircle(sketch, "E104.4", {"center": v(0, 50) * mm, "radius": 6.25 * mm});
            skCircle(sketch, "E104.5", {"center": v(0, 50) * mm, "radius": 4.5 * mm});
            skCircle(sketch, "E104.6", {"center": v(-25, 50) * mm, "radius": 6.25 * mm});
            skCircle(sketch, "E104.7", {"center": v(-25, 50) * mm, "radius": 4.5 * mm});
            skCircle(sketch, "E104.8", {"center": v(-50, 50) * mm, "radius": 6.25 * mm});
            skCircle(sketch, "E104.9", {"center": v(-50, 50) * mm, "radius": 4.5 * mm});
            skCircle(sketch, "E104.10", {"center": v(-50, 25) * mm, "radius": 6.25 * mm});
            skCircle(sketch, "E104.11", {"center": v(-50, 25) * mm, "radius": 4.5 * mm});
            skCircle(sketch, "E104.12", {"center": v(-50, 0) * mm, "radius": 6.25 * mm});
            skCircle(sketch, "E104.13", {"center": v(-50, 0) * mm, "radius": 4.5 * mm});
            skCircle(sketch, "E104.14", {"center": v(-50, -25) * mm, "radius": 6.25 * mm});
            skCircle(sketch, "E104.15", {"center": v(-50, -25) * mm, "radius": 4.5 * mm});
            skCircle(sketch, "E104.16", {"center": v(-50, -50) * mm, "radius": 6.25 * mm});
            skCircle(sketch, "E104.17", {"center": v(-50, -50) * mm, "radius": 4.5 * mm});
            skCircle(sketch, "E104.18", {"center": v(-25, -50) * mm, "radius": 6.25 * mm});
            skCircle(sketch, "E104.19", {"center": v(-25, -50) * mm, "radius": 4.5 * mm});
            skCircle(sketch, "E104.20", {"center": v(0, -50) * mm, "radius": 6.25 * mm});
            skCircle(sketch, "E104.21", {"center": v(0, -50) * mm, "radius": 4.5 * mm});
            skCircle(sketch, "E104.22", {"center": v(25, -50) * mm, "radius": 6.25 * mm});
            skCircle(sketch, "E104.23", {"center": v(25, -50) * mm, "radius": 4.5 * mm});
            skCircle(sketch, "E104.24", {"center": v(50, -50) * mm, "radius": 6.25 * mm});
            skCircle(sketch, "E104.25", {"center": v(50, -50) * mm, "radius": 4.5 * mm});
            skCircle(sketch, "E104.26", {"center": v(50, -25) * mm, "radius": 6.25 * mm});
            skCircle(sketch, "E104.27", {"center": v(50, -25) * mm, "radius": 4.5 * mm});
            skCircle(sketch, "E104.28", {"center": v(50, 0) * mm, "radius": 6.25 * mm});
            skCircle(sketch, "E104.29", {"center": v(50, 0) * mm, "radius": 4.5 * mm});
            skCircle(sketch, "E104.30", {"center": v(50, 25) * mm, "radius": 6.25 * mm});
            skCircle(sketch, "E104.31", {"center": v(50, 25) * mm, "radius": 4.5 * mm});
            skArc(sketch, "E105.0", {"start": v(-18.41, -26.17) * mm, "mid": v(-12.25, -29.56) * mm, "end": v(-5.49, -31.53) * mm});
            skArc(sketch, "E105.1", {"start": v(-21.87, -31.08) * mm, "mid": v(-14.54, -35.1) * mm, "end": v(-6.51, -37.44) * mm});
            skArc(sketch, "E105.2", {"start": v(6.51, -37.44) * mm, "mid": v(14.54, -35.1) * mm, "end": v(21.87, -31.08) * mm});
            skArc(sketch, "E105.3", {"start": v(5.49, -31.53) * mm, "mid": v(12.25, -29.56) * mm, "end": v(18.41, -26.17) * mm});
            skArc(sketch, "E105.4", {"start": v(31.08, -21.87) * mm, "mid": v(35.1, -14.54) * mm, "end": v(37.44, -6.51) * mm});
            skArc(sketch, "E105.5", {"start": v(26.17, -18.41) * mm, "mid": v(29.56, -12.25) * mm, "end": v(31.53, -5.49) * mm});
            skArc(sketch, "E105.6", {"start": v(31.53, -5.49) * mm, "mid": v(35, -3.04) * mm, "end": v(37.44, -6.51) * mm});
            skArc(sketch, "E105.7", {"start": v(31.08, -21.87) * mm, "mid": v(26.9, -22.6) * mm, "end": v(26.17, -18.41) * mm});
            skArc(sketch, "E105.8", {"start": v(18.41, -26.17) * mm, "mid": v(22.6, -26.9) * mm, "end": v(21.87, -31.08) * mm});
            skArc(sketch, "E105.9", {"start": v(6.51, -37.44) * mm, "mid": v(3.04, -35) * mm, "end": v(5.49, -31.53) * mm});
            skArc(sketch, "E105.10", {"start": v(-5.49, -31.53) * mm, "mid": v(-3.04, -35) * mm, "end": v(-6.51, -37.44) * mm});
            skArc(sketch, "E105.11", {"start": v(-21.87, -31.08) * mm, "mid": v(-22.6, -26.9) * mm, "end": v(-18.41, -26.17) * mm});
            skCircle(sketch, "E106.0", {"center": v(0, 0) * mm, "radius": 8.5 * mm});
            skCircle(sketch, "E106.1", {"center": v(0, -12.5) * mm, "radius": 1.5 * mm});
            skCircle(sketch, "E106.2", {"center": v(0, 12.5) * mm, "radius": 1.5 * mm});
            skCircle(sketch, "E106.3", {"center": v(-12.5, 0) * mm, "radius": 1.5 * mm});
            skCircle(sketch, "E106.4", {"center": v(12.5, 0) * mm, "radius": 1.5 * mm});
            skCircle(sketch, "E106.5", {"center": v(16, -16) * mm, "radius": 1.5 * mm});
            skCircle(sketch, "E106.6", {"center": v(0, -22.63) * mm, "radius": 1.5 * mm});
            skCircle(sketch, "E106.7", {"center": v(-16, -16) * mm, "radius": 1.5 * mm});
            skCircle(sketch, "E106.8", {"center": v(-22.63, 0) * mm, "radius": 1.5 * mm});
            skCircle(sketch, "E106.9", {"center": v(-16, 16) * mm, "radius": 1.5 * mm});
            skCircle(sketch, "E106.10", {"center": v(0, 22.63) * mm, "radius": 1.5 * mm});
            skCircle(sketch, "E106.11", {"center": v(16, 16) * mm, "radius": 1.5 * mm});
            skCircle(sketch, "E106.12", {"center": v(22.63, 0) * mm, "radius": 1.5 * mm});
            skLineSegment(sketch, "E107.0", {"start": v(-60.5, 60.5) * mm, "end": v(-60.5, -60.5) * mm});
            skLineSegment(sketch, "E107.1", {"start": v(-60.5, 60.5) * mm, "end": v(60.5, 60.5) * mm});
            skLineSegment(sketch, "E107.2", {"start": v(60.5, 60.5) * mm, "end": v(60.5, -60.5) * mm});
            skLineSegment(sketch, "E107.3", {"start": v(-60.5, -60.5) * mm, "end": v(60.5, -60.5) * mm});
            skSolve(sketch);
        }
        {
            var Q0;
            Q0=makeQuery(id+"F9.imprint","IMPRINT",FACE,{"disambiguationData":[TD([[makeQuery(id+"F9.imprint","IMPRINT",EDGE,{"derivedFrom":sQuery(id+"F9.wireOp",EDGE,"E102.10")}),-1.0]])]});
            extrude(context, id + "F10", {"entities" : qUnion([Q0]), "depth" : 3.75 * mm});
        }
        {
            var Q0;
            Q0=makeQuery(id+"F9.imprint","IMPRINT",FACE,{"disambiguationData":[TD([[makeQuery(id+"F9.imprint","IMPRINT",EDGE,{"derivedFrom":sQuery(id+"F9.wireOp",EDGE,"E104.8")}),1.0]])]});
            var Q1;
            Q1=makeQuery(id+"F9.imprint","IMPRINT",FACE,{"disambiguationData":[TD([[makeQuery(id+"F9.imprint","IMPRINT",EDGE,{"derivedFrom":sQuery(id+"F9.wireOp",EDGE,"E104.6")}),1.0]])]});
            var Q2;
            Q2=makeQuery(id+"F9.imprint","IMPRINT",FACE,{"disambiguationData":[TD([[makeQuery(id+"F9.imprint","IMPRINT",EDGE,{"derivedFrom":sQuery(id+"F9.wireOp",EDGE,"E104.4")}),1.0]])]});
            var Q3;
            Q3=makeQuery(id+"F9.imprint","IMPRINT",FACE,{"disambiguationData":[TD([[makeQuery(id+"F9.imprint","IMPRINT",EDGE,{"derivedFrom":sQuery(id+"F9.wireOp",EDGE,"E104.2")}),1.0]])]});
            var Q4;
            Q4=makeQuery(id+"F9.imprint","IMPRINT",FACE,{"disambiguationData":[TD([[makeQuery(id+"F9.imprint","IMPRINT",EDGE,{"derivedFrom":sQuery(id+"F9.wireOp",EDGE,"E104.0")}),1.0]])]});
            var Q5;
            Q5=makeQuery(id+"F9.imprint","IMPRINT",FACE,{"disambiguationData":[TD([[makeQuery(id+"F9.imprint","IMPRINT",EDGE,{"derivedFrom":sQuery(id+"F9.wireOp",EDGE,"E104.10")}),1.0]])]});
            var Q6;
            Q6=makeQuery(id+"F9.imprint","IMPRINT",FACE,{"disambiguationData":[TD([[makeQuery(id+"F9.imprint","IMPRINT",EDGE,{"derivedFrom":sQuery(id+"F9.wireOp",EDGE,"E104.30")}),1.0]])]});
            var Q7;
            Q7=makeQuery(id+"F9.imprint","IMPRINT",FACE,{"disambiguationData":[TD([[makeQuery(id+"F9.imprint","IMPRINT",EDGE,{"derivedFrom":sQuery(id+"F9.wireOp",EDGE,"E104.28")}),1.0]])]});
            var Q8;
            Q8=makeQuery(id+"F9.imprint","IMPRINT",FACE,{"disambiguationData":[TD([[makeQuery(id+"F9.imprint","IMPRINT",EDGE,{"derivedFrom":sQuery(id+"F9.wireOp",EDGE,"E104.26")}),1.0]])]});
            var Q9;
            Q9=makeQuery(id+"F9.imprint","IMPRINT",FACE,{"disambiguationData":[TD([[makeQuery(id+"F9.imprint","IMPRINT",EDGE,{"derivedFrom":sQuery(id+"F9.wireOp",EDGE,"E104.24")}),1.0]])]});
            var Q10;
            Q10=makeQuery(id+"F9.imprint","IMPRINT",FACE,{"disambiguationData":[TD([[makeQuery(id+"F9.imprint","IMPRINT",EDGE,{"derivedFrom":sQuery(id+"F9.wireOp",EDGE,"E104.22")}),1.0]])]});
            var Q11;
            Q11=makeQuery(id+"F9.imprint","IMPRINT",FACE,{"disambiguationData":[TD([[makeQuery(id+"F9.imprint","IMPRINT",EDGE,{"derivedFrom":sQuery(id+"F9.wireOp",EDGE,"E104.20")}),1.0]])]});
            var Q12;
            Q12=makeQuery(id+"F9.imprint","IMPRINT",FACE,{"disambiguationData":[TD([[makeQuery(id+"F9.imprint","IMPRINT",EDGE,{"derivedFrom":sQuery(id+"F9.wireOp",EDGE,"E104.18")}),1.0]])]});
            var Q13;
            Q13=makeQuery(id+"F9.imprint","IMPRINT",FACE,{"disambiguationData":[TD([[makeQuery(id+"F9.imprint","IMPRINT",EDGE,{"derivedFrom":sQuery(id+"F9.wireOp",EDGE,"E104.16")}),1.0]])]});
            var Q14;
            Q14=makeQuery(id+"F9.imprint","IMPRINT",FACE,{"disambiguationData":[TD([[makeQuery(id+"F9.imprint","IMPRINT",EDGE,{"derivedFrom":sQuery(id+"F9.wireOp",EDGE,"E104.14")}),1.0]])]});
            var Q15;
            Q15=makeQuery(id+"F9.imprint","IMPRINT",FACE,{"disambiguationData":[TD([[makeQuery(id+"F9.imprint","IMPRINT",EDGE,{"derivedFrom":sQuery(id+"F9.wireOp",EDGE,"E104.12")}),1.0]])]});
            extrude(context, id + "F11", {"entities" : qUnion([Q0, Q1, Q2, Q3, Q4, Q5, Q6, Q7, Q8, Q9, Q10, Q11, Q12, Q13, Q14, Q15]), "operationType" : NewBodyOperationType.ADD, "depth" : 2 * mm});
        }
        {
            var Q0;
            Q0=makeQuery(id+"F10.opExtrude","SWEPT_EDGE",EDGE,{"disambiguationData":[OSD([sQuery(id+"F9.wireOp",EDGE,"21158afe-6558-47d2-b588-9e2cb2e3cb2f.0"),sQuery(id+"F9.wireOp",EDGE,"21158afe-6558-47d2-b588-9e2cb2e3cb2f.3")])]});
            var Q1;
            Q1=makeQuery(id+"F10.opExtrude","SWEPT_EDGE",EDGE,{"disambiguationData":[OSD([sQuery(id+"F9.wireOp",EDGE,"21158afe-6558-47d2-b588-9e2cb2e3cb2f.2"),sQuery(id+"F9.wireOp",EDGE,"21158afe-6558-47d2-b588-9e2cb2e3cb2f.3")])]});
            var Q2;
            Q2=makeQuery(id+"F10.opExtrude","SWEPT_EDGE",EDGE,{"disambiguationData":[OSD([sQuery(id+"F9.wireOp",EDGE,"21158afe-6558-47d2-b588-9e2cb2e3cb2f.1"),sQuery(id+"F9.wireOp",EDGE,"21158afe-6558-47d2-b588-9e2cb2e3cb2f.2")])]});
            var Q3;
            Q3=makeQuery(id+"F10.opExtrude","SWEPT_EDGE",EDGE,{"disambiguationData":[OSD([sQuery(id+"F9.wireOp",EDGE,"21158afe-6558-47d2-b588-9e2cb2e3cb2f.0"),sQuery(id+"F9.wireOp",EDGE,"21158afe-6558-47d2-b588-9e2cb2e3cb2f.1")])]});
            var Q4;
            Q4=makeQuery(id+"F1.opExtrude","SWEPT_EDGE",EDGE,{"disambiguationData":[OSD([sQuery(id+"F0.wireOp",EDGE,"4bd72445-ccac-4010-9492-ce205e554f92.top"),sQuery(id+"F0.wireOp",EDGE,"4bd72445-ccac-4010-9492-ce205e554f92.right")])]});
            var Q5;
            Q5=makeQuery(id+"F1.opExtrude","SWEPT_EDGE",EDGE,{"disambiguationData":[OSD([sQuery(id+"F0.wireOp",EDGE,"1782753d-d1cd-43f3-90b6-b2e425ba2ceb.top"),sQuery(id+"F0.wireOp",EDGE,"1782753d-d1cd-43f3-90b6-b2e425ba2ceb.right")])]});
            var Q6;
            Q6=makeQuery(id+"F1.opExtrude","SWEPT_EDGE",EDGE,{"disambiguationData":[OSD([sQuery(id+"F0.wireOp",EDGE,"df5098c2-97dc-40db-a8c1-e7d122068beb0.MirrorCS"),sQuery(id+"F0.wireOp",EDGE,"da021dca-be56-4072-a210-eee63b100de80.MirrorCS")])]});
            var Q7;
            Q7=makeQuery(id+"F1.opExtrude","SWEPT_EDGE",EDGE,{"disambiguationData":[OSD([sQuery(id+"F0.wireOp",EDGE,"034febc5-2736-4d47-ad5d-1220d24f25580.MirrorCS"),sQuery(id+"F0.wireOp",EDGE,"7d6b432d-c6f7-4929-92ba-03f9c5655b390.MirrorCS")])]});
            var Q8;
            Q8=makeQuery(id+"F1.opExtrude","SWEPT_EDGE",EDGE,{"disambiguationData":[OSD([sQuery(id+"F0.wireOp",EDGE,"6e9c0fd7-de81-4499-9c2d-368c3a9eaf030.MirrorCS"),sQuery(id+"F0.wireOp",EDGE,"E62.MirrorCS")])]});
            var Q9;
            Q9=makeQuery(id+"F1.opExtrude","SWEPT_EDGE",EDGE,{"disambiguationData":[OSD([sQuery(id+"F0.wireOp",EDGE,"E61.right"),sQuery(id+"F0.wireOp",EDGE,"E63")])]});
            var Q10;
            Q10=makeQuery(id+"F1.opExtrude","SWEPT_EDGE",EDGE,{"disambiguationData":[OSD([sQuery(id+"F0.wireOp",EDGE,"E61.right"),sQuery(id+"F0.wireOp",EDGE,"E64")])]});
            fillet(context, id + "F12", {"entities" : qUnion([Q0, Q1, Q2, Q3, Q4, Q5, Q6, Q7, Q8, Q9, Q10]), "radius" : 10 * mm, "tangentPropagation" : true, "allowEdgeOverflow" : false});
        }
        {
            var Q0;
            Q0=makeQuery(id+"F6.imprint","IMPRINT",FACE,{"disambiguationData":[TD([[makeQuery(id+"F6.imprint","IMPRINT",EDGE,{"derivedFrom":sQuery(id+"F6.wireOp",EDGE,"E72.3")}),-1.0]])]});
            var Q1;
            Q1=makeQuery(id+"F6.imprint","IMPRINT",FACE,{"disambiguationData":[TD([[makeQuery(id+"F6.imprint","IMPRINT",EDGE,{"derivedFrom":sQuery(id+"F6.wireOp",EDGE,"E72.4")}),-1.0]])]});
            var Q2;
            Q2=makeQuery(id+"F6.imprint","IMPRINT",FACE,{"disambiguationData":[TD([[makeQuery(id+"F6.imprint","IMPRINT",EDGE,{"derivedFrom":sQuery(id+"F6.wireOp",EDGE,"E72.5")}),-1.0]])]});
            var Q3;
            Q3=makeQuery(id+"F6.imprint","IMPRINT",FACE,{"disambiguationData":[TD([[makeQuery(id+"F6.imprint","IMPRINT",EDGE,{"derivedFrom":sQuery(id+"F6.wireOp",EDGE,"E72.6")}),-1.0]])]});
            var Q4;
            Q4=makeQuery(id+"F6.imprint","IMPRINT",FACE,{"disambiguationData":[TD([[makeQuery(id+"F6.imprint","IMPRINT",EDGE,{"derivedFrom":sQuery(id+"F6.wireOp",EDGE,"E72.7")}),-1.0]])]});
            var Q5;
            Q5=makeQuery(id+"F6.imprint","IMPRINT",FACE,{"disambiguationData":[TD([[makeQuery(id+"F6.imprint","IMPRINT",EDGE,{"derivedFrom":sQuery(id+"F6.wireOp",EDGE,"E72.8")}),-1.0]])]});
            var Q6;
            Q6=makeQuery(id+"F6.imprint","IMPRINT",FACE,{"disambiguationData":[TD([[makeQuery(id+"F6.imprint","IMPRINT",EDGE,{"derivedFrom":sQuery(id+"F6.wireOp",EDGE,"E72.9")}),-1.0]])]});
            var Q7;
            Q7=makeQuery(id+"F6.imprint","IMPRINT",FACE,{"disambiguationData":[TD([[makeQuery(id+"F6.imprint","IMPRINT",EDGE,{"derivedFrom":sQuery(id+"F6.wireOp",EDGE,"E72.10")}),-1.0]])]});
            var Q8;
            Q8=makeQuery(id+"F6.imprint","IMPRINT",FACE,{"disambiguationData":[TD([[makeQuery(id+"F6.imprint","IMPRINT",EDGE,{"derivedFrom":sQuery(id+"F6.wireOp",EDGE,"E72.11")}),-1.0]])]});
            var Q9;
            Q9=makeQuery(id+"F6.imprint","IMPRINT",FACE,{"disambiguationData":[TD([[makeQuery(id+"F6.imprint","IMPRINT",EDGE,{"derivedFrom":sQuery(id+"F6.wireOp",EDGE,"E72.12")}),-1.0]])]});
            var Q10;
            Q10=makeQuery(id+"F6.imprint","IMPRINT",FACE,{"disambiguationData":[TD([[makeQuery(id+"F6.imprint","IMPRINT",EDGE,{"derivedFrom":sQuery(id+"F6.wireOp",EDGE,"E72.13")}),-1.0]])]});
            var Q11;
            Q11=makeQuery(id+"F6.imprint","IMPRINT",FACE,{"disambiguationData":[TD([[makeQuery(id+"F6.imprint","IMPRINT",EDGE,{"derivedFrom":sQuery(id+"F6.wireOp",EDGE,"E72.14")}),-1.0]])]});
            var Q12;
            Q12=makeQuery(id+"F6.imprint","IMPRINT",FACE,{"disambiguationData":[TD([[makeQuery(id+"F6.imprint","IMPRINT",EDGE,{"derivedFrom":sQuery(id+"F6.wireOp",EDGE,"E70.1")}),-1.0]])]});
            var Q13;
            Q13=makeQuery(id+"F6.imprint","IMPRINT",FACE,{"disambiguationData":[TD([[makeQuery(id+"F6.imprint","IMPRINT",EDGE,{"derivedFrom":sQuery(id+"F6.wireOp",EDGE,"E72.0")}),-1.0]])]});
            var Q14;
            Q14=makeQuery(id+"F6.imprint","IMPRINT",FACE,{"disambiguationData":[TD([[makeQuery(id+"F6.imprint","IMPRINT",EDGE,{"derivedFrom":sQuery(id+"F6.wireOp",EDGE,"E72.1")}),-1.0]])]});
            var Q15;
            Q15=makeQuery(id+"F6.imprint","IMPRINT",FACE,{"disambiguationData":[TD([[makeQuery(id+"F6.imprint","IMPRINT",EDGE,{"derivedFrom":sQuery(id+"F6.wireOp",EDGE,"E72.2")}),-1.0]])]});
            extrude(context, id + "F13", {"entities" : qUnion([Q0, Q1, Q2, Q3, Q4, Q5, Q6, Q7, Q8, Q9, Q10, Q11, Q12, Q13, Q14, Q15]), "operationType" : NewBodyOperationType.REMOVE, "oppositeDirection" : true, "depth" : 1 * mm});
        }
        {
            var Q0;
            Q0=makeQuery(id+"F10.opExtrude","SWEPT_EDGE",EDGE,{"disambiguationData":[OSD([sQuery(id+"F9.wireOp",EDGE,"E107.2"),sQuery(id+"F9.wireOp",EDGE,"E107.3")])]});
            var Q1;
            Q1=makeQuery(id+"F10.opExtrude","SWEPT_EDGE",EDGE,{"disambiguationData":[OSD([sQuery(id+"F9.wireOp",EDGE,"E107.0"),sQuery(id+"F9.wireOp",EDGE,"E107.3")])]});
            var Q2;
            Q2=makeQuery(id+"F10.opExtrude","SWEPT_EDGE",EDGE,{"disambiguationData":[OSD([sQuery(id+"F9.wireOp",EDGE,"E107.0"),sQuery(id+"F9.wireOp",EDGE,"E107.1")])]});
            var Q3;
            Q3=makeQuery(id+"F10.opExtrude","SWEPT_EDGE",EDGE,{"disambiguationData":[OSD([sQuery(id+"F9.wireOp",EDGE,"E107.1"),sQuery(id+"F9.wireOp",EDGE,"E107.2")])]});
            fillet(context, id + "F14", {"entities" : qUnion([Q0, Q1, Q2, Q3]), "radius" : 10 * mm, "tangentPropagation" : true, "allowEdgeOverflow" : false});
        }
    });
